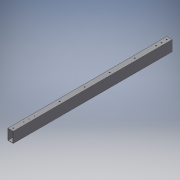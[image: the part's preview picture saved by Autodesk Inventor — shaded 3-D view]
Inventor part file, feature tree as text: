
AUTODESK INVENTOR PART (.ipt)
format: ipt  version: 2018 (Build 220112000, 112)  size: 175,616 bytes
history: native  units: in
note: dims shown in document units (in); Inventor stores cm internally (conversion verified against a paired STEP export)
features: extrude x5, sketch x5
ambient origin geometry x8: Origin, YZ Plane, XZ Plane, XY Plane, X Axis, Y Axis, Z Axis, Center Point
bodies: Solid1 (feature_tree)
feature tree (10):
  extrude  "Extrusion1"  Depth=2.0in
  sketch  "Sketch2"  dims[d2=0.0625in d3=30.0in d4=0.0in]
  extrude  "Extrusion4"  Depth=30.0in TaperAngle=0.0deg
  extrude  "Extrusion7"  Depth=4.724in
  extrude  "Extrusion8"  Depth=4.724in
  extrude  "Extrusion9"  Depth=1.0in
  sketch  "Sketch1"  dims[d0=1.0in d1=2.0in]
  sketch  "Sketch3"  dims[d5=4.543in d6=4.724in]
  sketch  "Sketch6"  dims[d7=4.724in d8=4.724in]
  sketch  "Sketch7"  dims[d9=4.724in d10=0.5in d11=1.0in d12=1.0in d13=1.0in d14=0.2031in d15=0.2031in d16=0.2031in d18=0.2031in d19=0.2031in d20=0.2031in d21=0.2031in d27=0.5in d28=0.2031in d29=20.6875in d30=0.0in d53=3.5in d54=1.0in d55=2.0in d56=0.2031in d57=4.25in d58=0.0in d59=4.25in d60=0.0in d61=0.2031in d62=0.2031in d63=2.0in d64=3.0in d65=1.125in d66=1.0in d67=0.0in]
